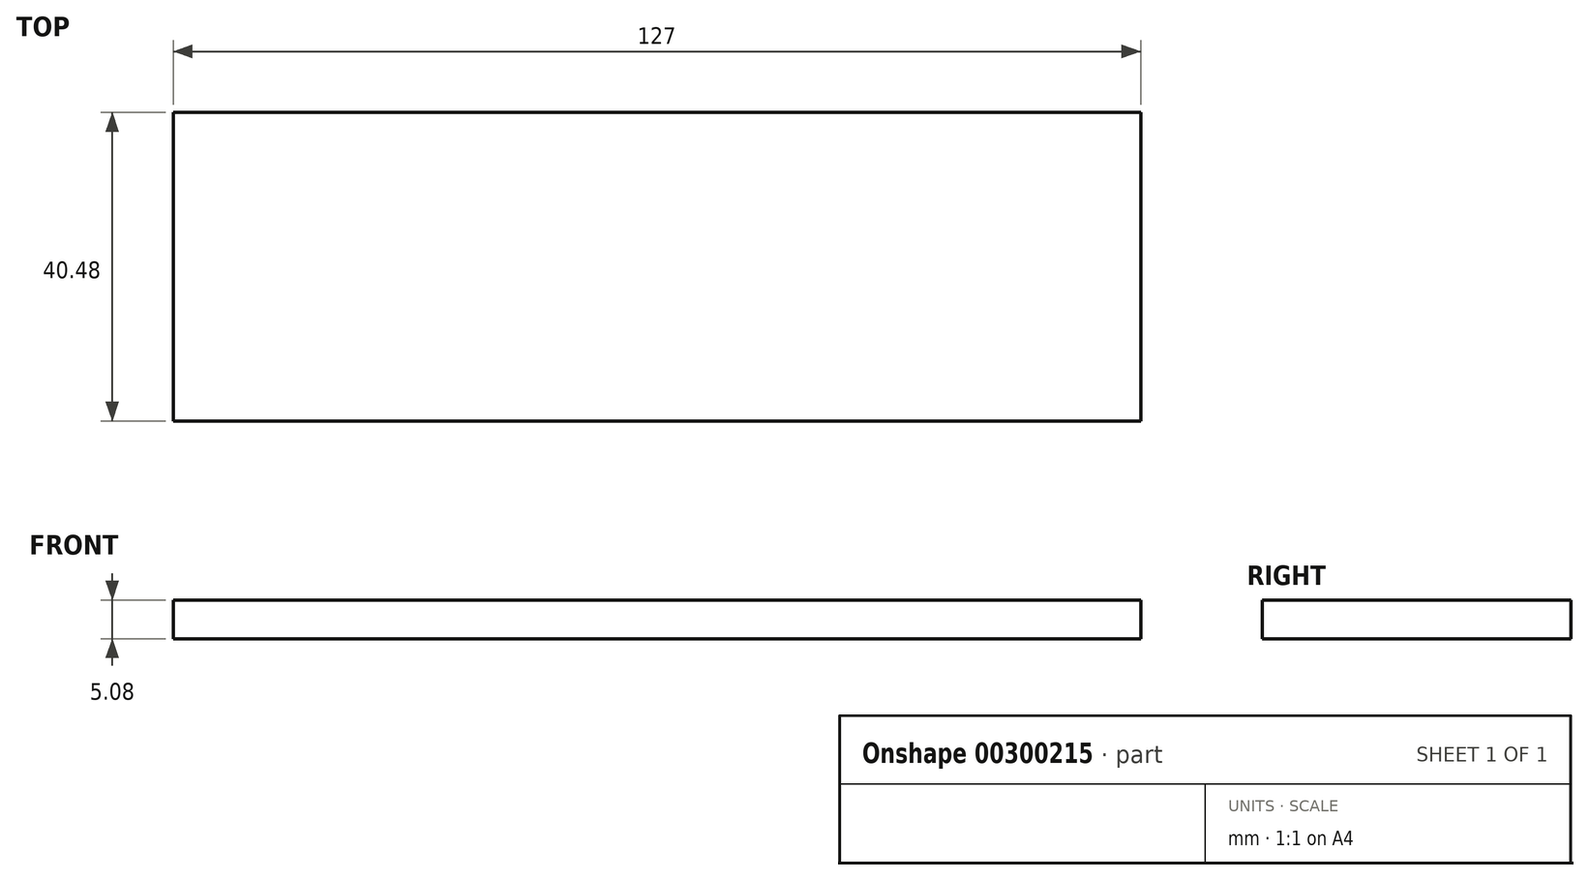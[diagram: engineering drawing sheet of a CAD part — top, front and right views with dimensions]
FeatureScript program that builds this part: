
annotation { "Feature Type Name" : "Feature", "Feature Type Description" : "" }
export const myFeature = defineFeature(function(context is Context, id is Id, definition is map)
    precondition{}
    {
        {
            var Q0;
            Q0=qCreatedBy(makeId("Top.planeOp"),FACE);
            var sketch = newSketch(context, id + "F0", { "sketchPlane" : qUnion([Q0])});
            skLineSegment(sketch, "E0.bottom", {"start": v(-61.3, -13.24) * mm, "end": v(65.7, -13.24) * mm});
            skLineSegment(sketch, "E0.top", {"start": v(-61.3, -53.72) * mm, "end": v(65.7, -53.72) * mm});
            skLineSegment(sketch, "E0.left", {"start": v(-61.3, -13.24) * mm, "end": v(-61.3, -53.72) * mm});
            skLineSegment(sketch, "E0.right", {"start": v(65.7, -13.24) * mm, "end": v(65.7, -53.72) * mm});
            skSolve(sketch);
        }
        {
            var Q0;
            Q0=makeQuery(id+"F0.imprint","IMPRINT",FACE,{"disambiguationData":[TD([[makeQuery(id+"F0.imprint","IMPRINT",EDGE,{"derivedFrom":sQuery(id+"F0.wireOp",EDGE,"E0.bottom")}),-1.0]])]});
            extrude(context, id + "F1", {"entities" : qUnion([Q0]), "depth" : 5.08 * mm});
        }
    });
